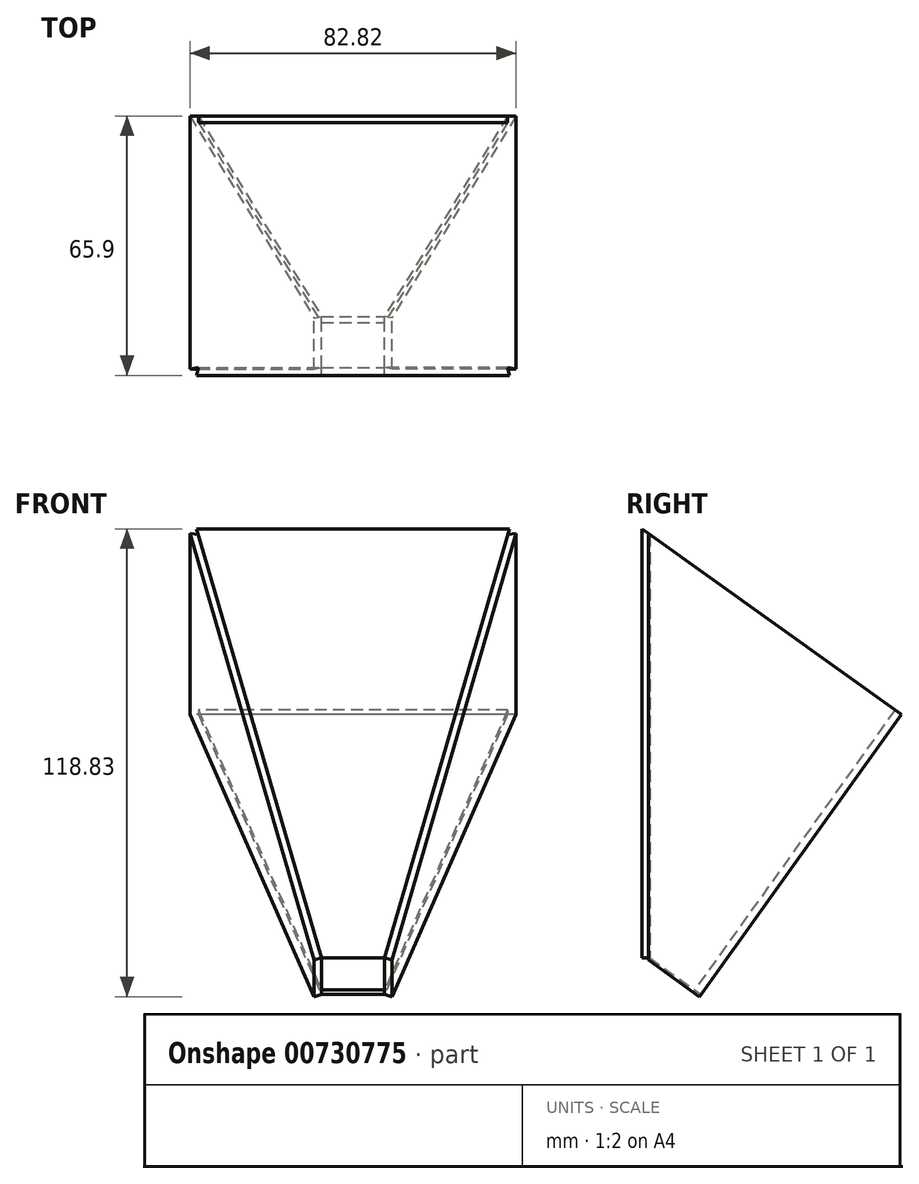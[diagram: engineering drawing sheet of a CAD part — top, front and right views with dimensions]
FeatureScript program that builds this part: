
annotation { "Feature Type Name" : "Feature", "Feature Type Description" : "" }
export const myFeature = defineFeature(function(context is Context, id is Id, definition is map)
    precondition{}
    {
        {
            assignVariable(context, id + "F0", {"name" : "wt", "anyValue" : 2});
        }
        {
            var Q0;
            Q0=qCreatedBy(makeId("Right.planeOp"),FACE);
            var sketch = newSketch(context, id + "F1", { "sketchPlane" : qUnion([Q0])});
            skLineSegment(sketch, "E0", {"start": v(0, 0) * mm, "end": v(0, -110) * mm});
            skLineSegment(sketch, "E1", {"start": v(0, -110) * mm, "end": v(13.01, -119.3) * mm});
            skLineSegment(sketch, "E2", {"start": v(13.01, -119.3) * mm, "end": v(65.07, -46.55) * mm});
            skLineSegment(sketch, "E3", {"start": v(65.07, -46.55) * mm, "end": v(0, 0) * mm});
            skSolve(sketch);
        }
        {
            var Q0;
            Q0=sQuery(id+"F1.wireOp",EDGE,"E3");
            cPlane(context, id + "F2", {"entities" : qUnion([Q0]), "cplaneType" : CPlaneType.LINE_ANGLE, "offset" : 25 * mm, "angle" : 0 * degree, "width" : 150 * mm, "height" : 150 * mm});
        }
        {
            var Q0;
            Q0=sQuery(id+"F1.wireOp",EDGE,"E1");
            cPlane(context, id + "F3", {"entities" : qUnion([Q0]), "cplaneType" : CPlaneType.LINE_ANGLE, "offset" : 25 * mm, "angle" : 0 * degree, "width" : 150 * mm, "height" : 150 * mm});
        }
        {
            var Q0;
            Q0=qCreatedBy(id+"F2.planeOp",FACE);
            var sketch = newSketch(context, id + "F4", { "sketchPlane" : qUnion([Q0])});
            skLineSegment(sketch, "E4", {"start": v(0, 0) * mm, "end": v(40, 0) * mm});
            skLineSegment(sketch, "E5.0", {"start": v(0, -80) * mm, "end": v(0, 0) * mm, "construction": true});
            skLineSegment(sketch, "E6", {"start": v(40, 0) * mm, "end": v(40, -80) * mm});
            skLineSegment(sketch, "E7", {"start": v(40, -80) * mm, "end": v(0, -80) * mm});
            skLineSegment(sketch, "E8.MirrorCS", {"start": v(0, 0) * mm, "end": v(-40, 0) * mm});
            skLineSegment(sketch, "E9.MirrorCS", {"start": v(-40, -80) * mm, "end": v(0, -80) * mm});
            skLineSegment(sketch, "E10.MirrorCS", {"start": v(-40, 0) * mm, "end": v(-40, -80) * mm});
            skSolve(sketch);
        }
        {
            var Q0;
            Q0=qCreatedBy(id+"F3.planeOp",FACE);
            var sketch = newSketch(context, id + "F5", { "sketchPlane" : qUnion([Q0])});
            skLineSegment(sketch, "E11.0", {"start": v(0, 64) * mm, "end": v(0, 80) * mm, "construction": true});
            skLineSegment(sketch, "E12", {"start": v(0, 64) * mm, "end": v(8, 64) * mm});
            skLineSegment(sketch, "E13", {"start": v(8, 64) * mm, "end": v(8, 80) * mm});
            skLineSegment(sketch, "E14", {"start": v(8, 80) * mm, "end": v(0, 80) * mm});
            skLineSegment(sketch, "E15.MirrorCS", {"start": v(0, 64) * mm, "end": v(-8, 64) * mm});
            skLineSegment(sketch, "E16.MirrorCS", {"start": v(-8, 64) * mm, "end": v(-8, 80) * mm});
            skLineSegment(sketch, "E17.MirrorCS", {"start": v(-8, 80) * mm, "end": v(0, 80) * mm});
            skSolve(sketch);
        }
        {
            var Q0;
            Q0=makeQuery(id+"F4.imprint","IMPRINT",FACE,{"disambiguationData":[TD([[makeQuery(id+"F4.imprint","IMPRINT",EDGE,{"derivedFrom":sQuery(id+"F4.wireOp",EDGE,"E4")}),-1.0]])]});
            var Q1;
            Q1=makeQuery(id+"F5.imprint","IMPRINT",FACE,{"disambiguationData":[TD([[makeQuery(id+"F5.imprint","IMPRINT",EDGE,{"derivedFrom":sQuery(id+"F5.wireOp",EDGE,"E12")}),1.0]])]});
            loft(context, id + "F6", {"sheetProfilesArray" : [{ "sheetProfileEntities" : qUnion([Q0]) }, { "sheetProfileEntities" : qUnion([Q1]) }]});
        }
        {
            var Q0;
            Q0=makeQuery(id+"F6.opLoft","SWEPT_FACE",FACE,{"disambiguationData":[OSD([sQuery(id+"F4.wireOp",EDGE,"E4"),sQuery(id+"F4.wireOp",EDGE,"E6"),sQuery(id+"F4.wireOp",EDGE,"E8.MirrorCS"),sQuery(id+"F5.wireOp",EDGE,"E12"),sQuery(id+"F5.wireOp",EDGE,"E13"),sQuery(id+"F5.wireOp",EDGE,"E15.MirrorCS")])]});
            var sketch = newSketch(context, id + "F7", { "sketchPlane" : qUnion([Q0])});
            skLineSegment(sketch, "E18.0", {"start": v(0, 0) * mm, "end": v(-40, 0) * mm});
            skLineSegment(sketch, "E18.1", {"start": v(0, 0) * mm, "end": v(40, 0) * mm});
            skLineSegment(sketch, "E18.2", {"start": v(40, 0) * mm, "end": v(8, -110) * mm});
            skLineSegment(sketch, "E18.3", {"start": v(-40, 0) * mm, "end": v(-8, -110) * mm});
            skLineSegment(sketch, "E18.4", {"start": v(8, -110) * mm, "end": v(-8, -110) * mm});
            skLineSegment(sketch, "E19", {"start": v(0, 0) * mm, "end": v(0, -110) * mm, "construction": true});
            skLineSegment(sketch, "E20", {"start": v(-31.27, -30) * mm, "end": v(31.27, -30) * mm});
            skCircle(sketch, "E21", {"center": v(-11, -15) * mm, "radius": 5 * mm});
            skLineSegment(sketch, "E22", {"start": v(-6, -15) * mm, "end": v(0, -15) * mm, "construction": true});
            skLineSegment(sketch, "E23", {"start": v(-7.43, -11.5) * mm, "end": v(0, -11.5) * mm});
            skLineSegment(sketch, "E24.MirrorCS", {"start": v(-7.43, -18.5) * mm, "end": v(0, -18.5) * mm});
            skLineSegment(sketch, "E25", {"start": v(0, -11.5) * mm, "end": v(0, 0) * mm});
            skLineSegment(sketch, "E26", {"start": v(0, -18.5) * mm, "end": v(0, -30) * mm});
            skCircle(sketch, "E27", {"center": v(-25.8, -7.8) * mm, "radius": 3.8 * mm});
            skLineSegment(sketch, "E28", {"start": v(-16, -15) * mm, "end": v(-35.64, -15) * mm, "construction": true});
            skCircle(sketch, "E29.MirrorC", {"center": v(-25.8, -22.2) * mm, "radius": 3.8 * mm});
            skCircle(sketch, "E30.MirrorC", {"center": v(25.8, -7.8) * mm, "radius": 3.8 * mm});
            skCircle(sketch, "E31.MirrorC", {"center": v(25.8, -22.2) * mm, "radius": 3.8 * mm});
            skLineSegment(sketch, "E32", {"start": v(-15.27, -85) * mm, "end": v(15.27, -85) * mm});
            skCircle(sketch, "E33", {"center": v(-5.5, -96.5) * mm, "radius": 3.5 * mm});
            skLineSegment(sketch, "E34", {"start": v(-2, -96.5) * mm, "end": v(0, -96.5) * mm, "construction": true});
            skLineSegment(sketch, "E35", {"start": v(-2.9, -94.15) * mm, "end": v(0, -94.15) * mm});
            skLineSegment(sketch, "E36.MirrorCS", {"start": v(-2.9, -98.85) * mm, "end": v(0, -98.85) * mm});
            skLineSegment(sketch, "E37", {"start": v(0, -94.15) * mm, "end": v(0, -85) * mm});
            skLineSegment(sketch, "E38", {"start": v(0, -98.85) * mm, "end": v(0, -110) * mm});
            skLineSegment(sketch, "E39", {"start": v(0, -85) * mm, "end": v(0, -30) * mm});
            skSolve(sketch);
        }
        {
            var Q0;
            {var subQ7=sQuery(id+"F7.wireOp",EDGE,"E18.1");Q0=makeQuery(id+"F7.imprint","IMPRINT",FACE,{"disambiguationData":[TD([[makeQuery(id+"F7.imprint","IMPRINT",EDGE,{"derivedFrom":subQ7}),1.0]])]});}
            var Q1;
            {var subQ0=sQuery(id+"F7.wireOp",EDGE,"E21");var subQ1=makeQuery(id+"F7.imprint","INTERSECT",VERTEX,{"derivedFrom":[subQ0,sQuery(id+"F7.wireOp",EDGE,"E23")]});Q1=makeQuery(id+"F7.imprint","IMPRINT",FACE,{"disambiguationData":[TD([[makeQuery(id+"F7.imprint","IMPRINT",EDGE,{"disambiguationData":[TD([[subQ1,-1.0]])],"derivedFrom":subQ0}),1.0]])]});}
            var Q2;
            {var subQ5=sQuery(id+"F7.wireOp",EDGE,"E39");Q2=makeQuery(id+"F7.imprint","IMPRINT",FACE,{"disambiguationData":[TD([[makeQuery(id+"F7.imprint","IMPRINT",EDGE,{"derivedFrom":subQ5}),-1.0]])]});}
            var Q3;
            {var subQ0=sQuery(id+"F7.wireOp",EDGE,"E35");Q3=makeQuery(id+"F7.imprint","IMPRINT",FACE,{"disambiguationData":[TD([[makeQuery(id+"F7.imprint","IMPRINT",EDGE,{"derivedFrom":subQ0}),-1.0]])]});}
            var Q4;
            {var subQ0=sQuery(id+"F7.wireOp",EDGE,"E33");var subQ1=makeQuery(id+"F7.imprint","INTERSECT",VERTEX,{"derivedFrom":[subQ0,sQuery(id+"F7.wireOp",EDGE,"E35")]});Q4=makeQuery(id+"F7.imprint","IMPRINT",FACE,{"disambiguationData":[TD([[makeQuery(id+"F7.imprint","IMPRINT",EDGE,{"disambiguationData":[TD([[subQ1,-1.0]])],"derivedFrom":subQ0}),1.0]])]});}
            extrude(context, id + "F8", {"entities" : qUnion([Q0, Q1, Q2, Q3, Q4]), "depth" : (getVariable(context, 'wt')) * mm, "offsetDistance" : 25 * mm});
        }
        {
            var Q0;
            {var subQ7=sQuery(id+"F7.wireOp",EDGE,"E18.0");Q0=makeQuery(id+"F7.imprint","IMPRINT",FACE,{"disambiguationData":[TD([[makeQuery(id+"F7.imprint","IMPRINT",EDGE,{"derivedFrom":subQ7}),1.0]])]});}
            var Q1;
            {var subQ5=sQuery(id+"F7.wireOp",EDGE,"E39");Q1=makeQuery(id+"F7.imprint","IMPRINT",FACE,{"disambiguationData":[TD([[makeQuery(id+"F7.imprint","IMPRINT",EDGE,{"derivedFrom":subQ5}),1.0]])]});}
            var Q2;
            {var subQ0=sQuery(id+"F7.wireOp",EDGE,"E35");Q2=makeQuery(id+"F7.imprint","IMPRINT",FACE,{"disambiguationData":[TD([[makeQuery(id+"F7.imprint","IMPRINT",EDGE,{"derivedFrom":subQ0}),1.0]])]});}
            extrude(context, id + "F9", {"entities" : qUnion([Q0, Q1, Q2]), "depth" : (getVariable(context, 'wt')) * mm, "offsetDistance" : 25 * mm});
        }
        {
            var Q0;
            Q0=makeQuery(id+"F6.opLoft","SWEPT_FACE",FACE,{"disambiguationData":[OSD([sQuery(id+"F4.wireOp",EDGE,"E4"),sQuery(id+"F4.wireOp",EDGE,"E6"),sQuery(id+"F4.wireOp",EDGE,"E7"),sQuery(id+"F5.wireOp",EDGE,"E12"),sQuery(id+"F5.wireOp",EDGE,"E13"),sQuery(id+"F5.wireOp",EDGE,"E14")])]});
            extrude(context, id + "F10", {"entities" : qUnion([Q0]), "depth" : (getVariable(context, 'wt')) * mm, "offsetDistance" : 25 * mm});
        }
        {
            var Q0;
            Q0=makeQuery(id+"F6.opLoft","SWEPT_FACE",FACE,{"disambiguationData":[OSD([sQuery(id+"F4.wireOp",EDGE,"E8.MirrorCS"),sQuery(id+"F4.wireOp",EDGE,"E9.MirrorCS"),sQuery(id+"F4.wireOp",EDGE,"E10.MirrorCS"),sQuery(id+"F5.wireOp",EDGE,"E15.MirrorCS"),sQuery(id+"F5.wireOp",EDGE,"E16.MirrorCS"),sQuery(id+"F5.wireOp",EDGE,"E17.MirrorCS")])]});
            extrude(context, id + "F11", {"entities" : qUnion([Q0]), "depth" : (getVariable(context, 'wt')) * mm, "offsetDistance" : 25 * mm});
        }
        {
            var Q0;
            Q0=makeQuery(id+"F6.opLoft","SWEPT_FACE",FACE,{"disambiguationData":[OSD([sQuery(id+"F4.wireOp",EDGE,"E7"),sQuery(id+"F4.wireOp",EDGE,"E9.MirrorCS"),sQuery(id+"F4.wireOp",EDGE,"E10.MirrorCS"),sQuery(id+"F5.wireOp",EDGE,"E14"),sQuery(id+"F5.wireOp",EDGE,"E16.MirrorCS"),sQuery(id+"F5.wireOp",EDGE,"E17.MirrorCS")])]});
            extrude(context, id + "F12", {"entities" : qUnion([Q0]), "oppositeDirection" : true, "depth" : (getVariable(context, 'wt')) * mm, "offsetDistance" : 25 * mm});
        }
        {
            var Q0;
            Q0=makeQuery(id+"F6.opLoft","SWEPT_FACE",FACE,{"disambiguationData":[OSD([sQuery(id+"F4.wireOp",EDGE,"E4"),sQuery(id+"F4.wireOp",EDGE,"E6"),sQuery(id+"F4.wireOp",EDGE,"E8.MirrorCS"),sQuery(id+"F5.wireOp",EDGE,"E12"),sQuery(id+"F5.wireOp",EDGE,"E13"),sQuery(id+"F5.wireOp",EDGE,"E15.MirrorCS")])]});
            extrude(context, id + "F13", {"entities" : qUnion([Q0]), "oppositeDirection" : true, "depth" : (getVariable(context, 'wt')) * mm, "offsetDistance" : 25 * mm});
        }
        {
            var Q0;
            Q0=makeQuery(id+"F6.opLoft","SWEPT_FACE",FACE,{"disambiguationData":[OSD([sQuery(id+"F4.wireOp",EDGE,"E4"),sQuery(id+"F4.wireOp",EDGE,"E6"),sQuery(id+"F4.wireOp",EDGE,"E8.MirrorCS"),sQuery(id+"F5.wireOp",EDGE,"E12"),sQuery(id+"F5.wireOp",EDGE,"E13"),sQuery(id+"F5.wireOp",EDGE,"E15.MirrorCS")])]});
            extrude(context, id + "F14", {"entities" : qUnion([Q0]), "operationType" : NewBodyOperationType.ADD, "depth" : (getVariable(context, 'wt')) * mm, "offsetDistance" : 25 * mm});
        }
        {
            var Q0;
            Q0=makeQuery(id+"F12.opExtrude","CAP_FACE",FACE,{"disambiguationData":[OSD([sQuery(id+"F4.wireOp",EDGE,"E7"),sQuery(id+"F4.wireOp",EDGE,"E9.MirrorCS"),sQuery(id+"F4.wireOp",EDGE,"E10.MirrorCS"),sQuery(id+"F5.wireOp",EDGE,"E14"),sQuery(id+"F5.wireOp",EDGE,"E16.MirrorCS"),sQuery(id+"F5.wireOp",EDGE,"E17.MirrorCS")])],"isStart":true});
            var sketch = newSketch(context, id + "F15", { "sketchPlane" : qUnion([Q0])});
            skLineSegment(sketch, "E40", {"start": v(-40, 0) * mm, "end": v(-50.7, 0) * mm});
            skLineSegment(sketch, "E41", {"start": v(50.57, 0) * mm, "end": v(40, 0) * mm});
            skLineSegment(sketch, "E42", {"start": v(-50.7, 0) * mm, "end": v(-50.7, -2) * mm});
            skLineSegment(sketch, "E43", {"start": v(-50.7, -2) * mm, "end": v(50.57, -2) * mm});
            skLineSegment(sketch, "E44", {"start": v(50.57, -2) * mm, "end": v(50.57, 0) * mm});
            skLineSegment(sketch, "E45", {"start": v(-50.7, 0) * mm, "end": v(-50.7, 4.75) * mm});
            skLineSegment(sketch, "E46", {"start": v(-50.7, 4.75) * mm, "end": v(50.57, 4.75) * mm});
            skLineSegment(sketch, "E47", {"start": v(50.57, 4.75) * mm, "end": v(50.57, 0) * mm});
            skSolve(sketch);
        }
        {
            var Q0;
            {var subQ1=sQuery(id+"F4.wireOp",EDGE,"E7");var subQ4=sQuery(id+"F4.wireOp",EDGE,"E10.MirrorCS");var subQ5=sQuery(id+"F4.wireOp",EDGE,"E9.MirrorCS");var subQ8=makeQuery(id+"F12.opExtrude","CAP_EDGE",EDGE,{"disambiguationData":[OSD([subQ1,subQ5,subQ4])],"isStart":true});Q0=makeQuery(id+"F15.imprint","IMPRINT",FACE,{"disambiguationData":[TD([[makeQuery(id+"F15.imprint","IMPRINT",EDGE,{"derivedFrom":subQ8}),1.0]])]});}
            var Q1;
            {var subQ0=sQuery(id+"F15.wireOp",EDGE,"E40");Q1=makeQuery(id+"F15.imprint","IMPRINT",FACE,{"disambiguationData":[TD([[makeQuery(id+"F15.imprint","IMPRINT",EDGE,{"derivedFrom":subQ0}),1.0]])]});}
            var Q2;
            {var subQ0=sQuery(id+"F15.wireOp",EDGE,"E41");Q2=makeQuery(id+"F15.imprint","IMPRINT",FACE,{"disambiguationData":[TD([[makeQuery(id+"F15.imprint","IMPRINT",EDGE,{"derivedFrom":subQ0}),1.0]])]});}
            var Q3;
            Q3=makeQuery(id+"F15.imprint","IMPRINT",FACE,{"disambiguationData":[TD([[makeQuery(id+"F15.imprint","IMPRINT",EDGE,{"derivedFrom":sQuery(id+"F15.wireOp",EDGE,"E40")}),-1.0]])]});
            extrude(context, id + "F16", {"entities" : qUnion([Q0, Q1, Q2, Q3]), "operationType" : NewBodyOperationType.REMOVE, "oppositeDirection" : true, "depth" : 90 * mm, "offsetDistance" : 25 * mm});
        }
    });
